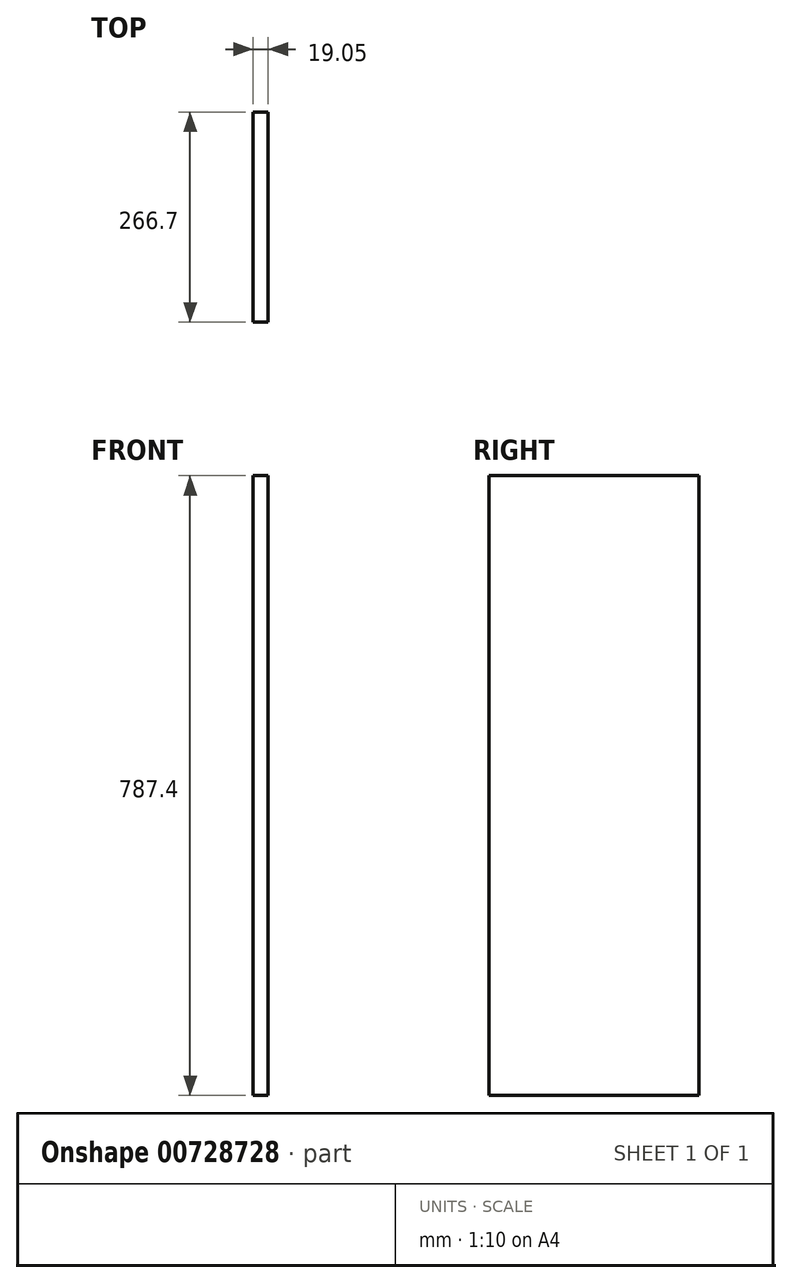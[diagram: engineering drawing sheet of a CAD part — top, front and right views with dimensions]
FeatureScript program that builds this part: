
annotation { "Feature Type Name" : "Feature", "Feature Type Description" : "" }
export const myFeature = defineFeature(function(context is Context, id is Id, definition is map)
    precondition{}
    {
        {
            var Q0;
            Q0=qCreatedBy(makeId("Right.planeOp"),FACE);
            var sketch = newSketch(context, id + "F0", { "sketchPlane" : qUnion([Q0])});
            skLineSegment(sketch, "E0.bottom", {"start": v(133.35, 393.7) * mm, "end": v(-133.35, 393.7) * mm});
            skLineSegment(sketch, "E0.top", {"start": v(133.35, -393.7) * mm, "end": v(-133.35, -393.7) * mm});
            skLineSegment(sketch, "E0.left", {"start": v(133.35, 393.7) * mm, "end": v(133.35, -393.7) * mm});
            skLineSegment(sketch, "E0.right", {"start": v(-133.35, 393.7) * mm, "end": v(-133.35, -393.7) * mm});
            skPoint(sketch, "E0.middle", {"position": v(0, 0) * mm});
            skSolve(sketch);
        }
        {
            var Q0;
            Q0 = qSketchRegion(id + "F0", true);
            extrude(context, id + "F1", {"entities" : qUnion([Q0]), "depth" : 19.05 * mm, "offsetDistance" : 25.4 * mm});
        }
    });
